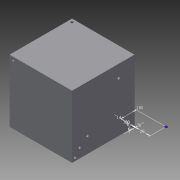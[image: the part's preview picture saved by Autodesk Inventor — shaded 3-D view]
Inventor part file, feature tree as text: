
AUTODESK INVENTOR PART (.ipt)
format: ipt  version: 2014 (Build 180170000, 170)  size: 243,200 bytes
history: native  units: mm
features: other x56, sketch x13, extrude x5
ambient origin geometry x8: Origin, YZ Plane, XZ Plane, XY Plane, X Axis, Y Axis, Z Axis, Center Point
bodies: 实体1 (feature_tree)
feature tree (74):
  extrude  "拉伸1"  Depth=50.0mm
  other  "UCS1"
  other  "UCS2"
  other  "UCS3"
  other  "UCS4"
  other  "UCS5"
  other  "UCS6"
  extrude  "拉伸2"  Depth=14.0mm
  extrude  "拉伸3"  Depth=44.0mm
  extrude  "拉伸4"  Depth=44.0mm
  extrude  "拉伸5"  Depth=32.0mm
  other  "iFeature13:26"
  other  "iFeature13:27"
  other  "iFeature13:28"
  other  "iFeature13:29"
  other  "iFeature13:30"
  other  "iFeature13:31"
  other  "iFeature13:32"
  other  "iFeature13:33"
  sketch  "草图1"  dims[d0=400.0mm d1=0.0mm]
  sketch  "草图2"  dims[d2=0.0mm d3=0.0mm d4=0.0mm d5=0.0mm d6=0.0mm d7=0.0mm]
  sketch  "草图3"  dims[d8=0.0mm d9=0.0mm d10=0.0mm d11=0.0mm d12=0.0mm d13=0.0mm]
  sketch  "草图4"  dims[d14=0.0mm d15=0.0mm d16=0.0mm d17=0.0mm d18=0.0mm d19=0.0mm]
  sketch  "草图8"  dims[d20=0.0mm d21=0.0mm d22=0.0mm d23=0.0mm d24=0.0mm d25=0.0mm]
  other  "UCS1: YZ 平面"
  other  "UCS1: XZ 平面"
  other  "UCS1: XY 平面"
  other  "UCS1: X 轴"
  other  "UCS1: Y 轴"
  other  "UCS1: Z 轴"
  other  "UCS1: 原点"
  other  "UCS2: YZ 平面"
  other  "UCS2: XZ 平面"
  other  "UCS2: XY 平面"
  other  "UCS2: X 轴"
  other  "UCS2: Y 轴"
  other  "UCS2: Z 轴"
  other  "UCS2: 原点"
  other  "UCS3: YZ 平面"
  other  "UCS3: XZ 平面"
  other  "UCS3: XY 平面"
  other  "UCS3: X 轴"
  other  "UCS3: Y 轴"
  other  "UCS3: Z 轴"
  other  "UCS3: 原点"
  other  "UCS4: YZ 平面"
  other  "UCS4: XZ 平面"
  other  "UCS4: XY 平面"
  other  "UCS4: X 轴"
  other  "UCS4: Y 轴"
  other  "UCS4: Z 轴"
  other  "UCS4: 原点"
  other  "UCS5: YZ 平面"
  other  "UCS5: XZ 平面"
  other  "UCS5: XY 平面"
  other  "UCS5: X 轴"
  other  "UCS5: Y 轴"
  other  "UCS5: Z 轴"
  other  "UCS5: 原点"
  other  "UCS6: YZ 平面"
  other  "UCS6: XZ 平面"
  other  "UCS6: XY 平面"
  other  "UCS6: X 轴"
  other  "UCS6: Y 轴"
  other  "UCS6: Z 轴"
  other  "UCS6: 原点"
  sketch  "草图34"  dims[d26=0.0mm d27=0.0mm d28=0.0mm d29=0.0mm d30=0.0mm d31=0.0mm]
  sketch  "草图35"  dims[d32=0.0mm d33=0.0mm d34=0.0mm d35=0.0mm d36=0.0mm d37=0.0mm d38=50.0mm]
  sketch  "草图36"  dims[d39=60.0mm d42=14.0mm]
  sketch  "草图37"  dims[d43=44.0mm d44=0.0mm d45=44.0mm d46=-10.297443mm]
  sketch  "草图38"  dims[d47=44.0mm d48=-10.297443mm d64=16.0mm]
  sketch  "草图39"  dims[d65=32.0mm d66=0.0mm d132=100.0mm]
  sketch  "草图40"  dims[d133=80.0mm]
  sketch  "草图41"
